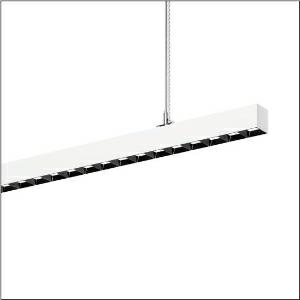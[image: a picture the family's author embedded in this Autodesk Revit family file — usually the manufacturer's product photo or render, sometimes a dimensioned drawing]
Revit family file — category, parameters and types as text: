
# Revit family: silica_21_51mx32dc4dwb
name_source: partatom
category: Lighting Fixtures
units: mm (PartAtom-declared; Revit-internal decimal feet)

## family parameters
Cut with Voids When Loaded = No
Host = Face
Light Source = No
Part Type = Normal
Room Calculation Point = No
Round Connector Dimension = Use Diameter
Shared = No

## types (1)
- --- (1 x LED, 18230 lm, 105.8 W, 4000K)
    Apparent Load = 106 VA
    CIE Flux Codes = 86 99 100 59 100
    Color Rendering = 80
    Color Temperature = 4000K
    Default Elevation = 1800 mm
    Description = Silica 21, office luminaire, primary light control with darklight reflector, of PMMA, black, CAT 2 (L<= 3000cd/m²), light emission: direct/indirect distribution, primary light characteristic: symmetric, installation type: suspended mounting, LED, rated luminous flux: 18.230lm, luminous efficacy: 172lm/W, light colour: 840, colour temperature: 4000K, control gear: DALI 2, with terminal, 3+2-pole, max. 2.5mm², mains connection: 220..240V, AC, 50/60Hz, rated input power: 105.8W, luminaire housing, of aluminium, traffic white (RAL 9016), length: 3.004mm, width: 53mm, height: 53mm, protection rating (complete): IP20, insulation class (complete): insulation class I (protective earthing), certification: CE, permissible operating ambient temperature: 0..+35°C, standard: EN 50419, packaging unit: 1 piece
    Height = 53 mm
    Lamp = 1 x LED
    Lamp Light Flux = 18230 lm
    Lamp Power = 105.8 W
    Lamp count = 1
    Length = 3004 mm
    Luminous efficacy = 172 lm/W
    Manufacturer = Siteco
    ModVariant = No
    Model = 51MX32DC4DWB
    Mounting Place = Ceiling
    Mounting Type = Pendant
    Number of Poles = 1
    OnlyDefault = Yes
    Power Factor = 1
    Product Name = Silica 21
    Product group = office luminaire | ceiling pendant
    ProductGroupID = 903
    Protection Class = Protection class I
    Protection Degree = IP 20
    RLX_Detail_Level = 1
    RLX_Emergency_Light_Flux = 0 lm
    RLX_Emergency_Type = 0
    RLX_Emergency_Type_DB = No
    RlxData = <blob elided: 64441 chars, md5=efd82966>
    Socket = socket
    Standby Power = 0 W
    System Light Flux = 18230 lm
    System Power = 106 W
    Type Comments = factory setting: luminous flux: 100 % | dim-lin: 254 | 366 mA
    Type Image = l_1335871.jpg
    URL = http://relux.com
    VarID = @adj_122403
    Voltage = 0 V
    Weight = 0.00 kg
    Width = 53 mm

## geometry (parser evidence)
native form markers: Blend x4, Sweep x14
no freeform markers — native parametric forms only
